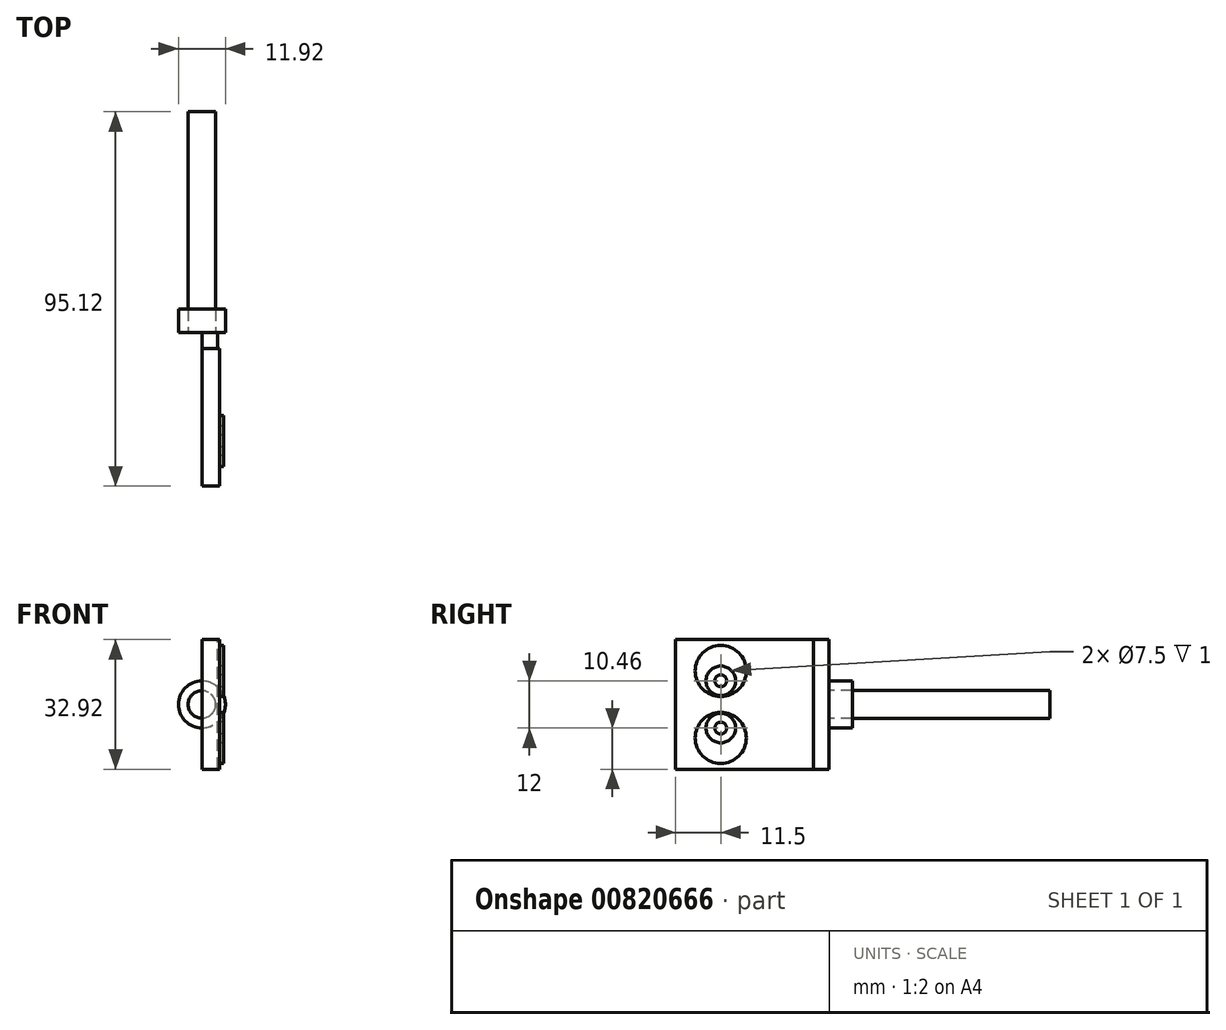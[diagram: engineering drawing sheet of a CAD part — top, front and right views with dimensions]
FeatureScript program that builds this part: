
annotation { "Feature Type Name" : "Feature", "Feature Type Description" : "" }
export const myFeature = defineFeature(function(context is Context, id is Id, definition is map)
    precondition{}
    {
        {
            var Q0;
            Q0=qCreatedBy(makeId("Front.planeOp"),FACE);
            var sketch = newSketch(context, id + "F0", { "sketchPlane" : qUnion([Q0])});
            skCircle(sketch, "E0", {"center": v(0, 0) * mm, "radius": 3.5 * mm});
            skLineSegment(sketch, "E1", {"start": v(0, 0) * mm, "end": v(3.5, 0) * mm});
            skSolve(sketch);
        }
        {
            var Q0;
            Q0=qCreatedBy(makeId("Top.planeOp"),FACE);
            var sketch = newSketch(context, id + "F1", { "sketchPlane" : qUnion([Q0])});
            skLineSegment(sketch, "E2", {"start": v(0, 0) * mm, "end": v(0, 56.12) * mm});
            skLineSegment(sketch, "E3", {"start": v(3.5, 0) * mm, "end": v(3.5, 56.12) * mm});
            skLineSegment(sketch, "E4", {"start": v(0, 0) * mm, "end": v(3.5, 0) * mm});
            skLineSegment(sketch, "E5", {"start": v(0, 56.12) * mm, "end": v(3.5, 56.12) * mm});
            skSolve(sketch);
        }
        {
            var Q0;
            Q0=makeQuery(id+"F1.imprint","IMPRINT",FACE,{"disambiguationData":[TD([[makeQuery(id+"F1.imprint","IMPRINT",EDGE,{"derivedFrom":sQuery(id+"F1.wireOp",EDGE,"E2")}),-1.0]])]});
            var Q1;
            Q1=sQuery(id+"F1.wireOp",EDGE,"E2");
            revolve(context, id + "F2", {"surfaceOperationType" : NewSurfaceOperationType.NEW, "entities" : qUnion([Q0]), "axis" : qUnion([Q1]), "revolveType" : RevolveType.FULL});
        }
        {
            var Q0;
            Q0=qCreatedBy(makeId("Front.planeOp"),FACE);
            var sketch = newSketch(context, id + "F3", { "sketchPlane" : qUnion([Q0])});
            skCircle(sketch, "E6", {"center": v(0, 0) * mm, "radius": 5.96 * mm});
            skSolve(sketch);
        }
        {
            var Q0;
            Q0=makeQuery(id+"F3.imprint","IMPRINT",FACE,{"disambiguationData":[TD([[makeQuery(id+"F3.imprint","IMPRINT",EDGE,{"derivedFrom":sQuery(id+"F3.wireOp",EDGE,"E6")}),1.0]])]});
            extrude(context, id + "F4", {"entities" : qUnion([Q0]), "oppositeDirection" : true, "depth" : 6 * mm, "offsetDistance" : 25 * mm});
        }
        {
            var Q0;
            Q0=qCreatedBy(makeId("Right.planeOp"),FACE);
            var sketch = newSketch(context, id + "F5", { "sketchPlane" : qUnion([Q0])});
            skLineSegment(sketch, "E7.bottom", {"start": v(0, -16.46) * mm, "end": v(-4, -16.46) * mm});
            skLineSegment(sketch, "E7.top", {"start": v(0, 16.46) * mm, "end": v(-4, 16.46) * mm});
            skLineSegment(sketch, "E7.left", {"start": v(0, -16.46) * mm, "end": v(0, 16.46) * mm});
            skLineSegment(sketch, "E7.right", {"start": v(-4, -16.46) * mm, "end": v(-4, 16.46) * mm});
            skLineSegment(sketch, "E8", {"start": v(0, 0) * mm, "end": v(0, 5.96) * mm});
            skLineSegment(sketch, "E9", {"start": v(0, 0) * mm, "end": v(0, -5.96) * mm});
            skSolve(sketch);
        }
        {
            var Q0;
            Q0=qCreatedBy(makeId("Right.planeOp"),FACE);
            var sketch = newSketch(context, id + "F6", { "sketchPlane" : qUnion([Q0])});
            skLineSegment(sketch, "E10.bottom", {"start": v(-4, 16.46) * mm, "end": v(-39, 16.46) * mm});
            skLineSegment(sketch, "E10.top", {"start": v(-4, -16.46) * mm, "end": v(-39, -16.46) * mm});
            skLineSegment(sketch, "E10.left", {"start": v(-4, 16.46) * mm, "end": v(-4, -16.46) * mm});
            skLineSegment(sketch, "E10.right", {"start": v(-39, 16.46) * mm, "end": v(-39, -16.46) * mm});
            skSolve(sketch);
        }
        {
            var Q0;
            {var subQ3=sQuery(id+"F5.wireOp",EDGE,"E7.bottom");Q0=makeQuery(id+"F5.imprint","IMPRINT",FACE,{"disambiguationData":[TD([[makeQuery(id+"F5.imprint","IMPRINT",EDGE,{"derivedFrom":subQ3}),-1.0]])]});}
            extrude(context, id + "F7", {"entities" : qUnion([Q0]), "depth" : 4 * mm, "offsetDistance" : 25 * mm});
        }
        {
            var Q0;
            Q0 = qSketchRegion(id + "F6", true);
            extrude(context, id + "F8", {"entities" : qUnion([Q0]), "depth" : 4.5 * mm, "offsetDistance" : 25 * mm});
        }
        {
            var Q0;
            Q0=makeQuery(id+"F8.opExtrude","CAP_FACE",FACE,{"disambiguationData":[OSD([sQuery(id+"F6.wireOp",EDGE,"E10.bottom"),sQuery(id+"F6.wireOp",EDGE,"E10.top"),sQuery(id+"F6.wireOp",EDGE,"E10.left"),sQuery(id+"F6.wireOp",EDGE,"E10.right")])],"isStart":false});
            var sketch = newSketch(context, id + "F9", { "sketchPlane" : qUnion([Q0])});
            skCircle(sketch, "E11", {"center": v(-27.5, 8.5) * mm, "radius": 6.5 * mm});
            skCircle(sketch, "E12", {"center": v(-27.5, -8.5) * mm, "radius": 6.5 * mm});
            skCircle(sketch, "E13", {"center": v(-27.5, -6) * mm, "radius": 3.75 * mm});
            skCircle(sketch, "E14", {"center": v(-27.5, 6) * mm, "radius": 3.75 * mm});
            skCircle(sketch, "E15", {"center": v(-27.5, -6) * mm, "radius": 1.5 * mm});
            skCircle(sketch, "E16", {"center": v(-27.5, 6) * mm, "radius": 1.5 * mm});
            skSolve(sketch);
        }
        {
            var Q0;
            Q0=makeQuery(id+"F9.imprint","IMPRINT",FACE,{"disambiguationData":[TD([[makeQuery(id+"F9.imprint","IMPRINT",EDGE,{"derivedFrom":sQuery(id+"F9.wireOp",EDGE,"E12")}),1.0]])]});
            var Q1;
            Q1=makeQuery(id+"F9.imprint","IMPRINT",FACE,{"disambiguationData":[TD([[makeQuery(id+"F9.imprint","IMPRINT",EDGE,{"derivedFrom":sQuery(id+"F9.wireOp",EDGE,"E11")}),1.0]])]});
            extrude(context, id + "F10", {"entities" : qUnion([Q0, Q1]), "operationType" : NewBodyOperationType.ADD, "depth" : 1 * mm, "offsetDistance" : 25 * mm});
        }
        {
            var Q0;
            Q0=makeQuery(id+"F9.imprint","IMPRINT",FACE,{"disambiguationData":[TD([[makeQuery(id+"F9.imprint","IMPRINT",EDGE,{"derivedFrom":sQuery(id+"F9.wireOp",EDGE,"E15")}),1.0]])]});
            var Q1;
            Q1=makeQuery(id+"F9.imprint","IMPRINT",FACE,{"disambiguationData":[TD([[makeQuery(id+"F9.imprint","IMPRINT",EDGE,{"derivedFrom":sQuery(id+"F9.wireOp",EDGE,"E16")}),1.0]])]});
            extrude(context, id + "F11", {"entities" : qUnion([Q0, Q1]), "operationType" : NewBodyOperationType.ADD, "depth" : 1 * mm, "offsetDistance" : 25 * mm});
        }
    });
